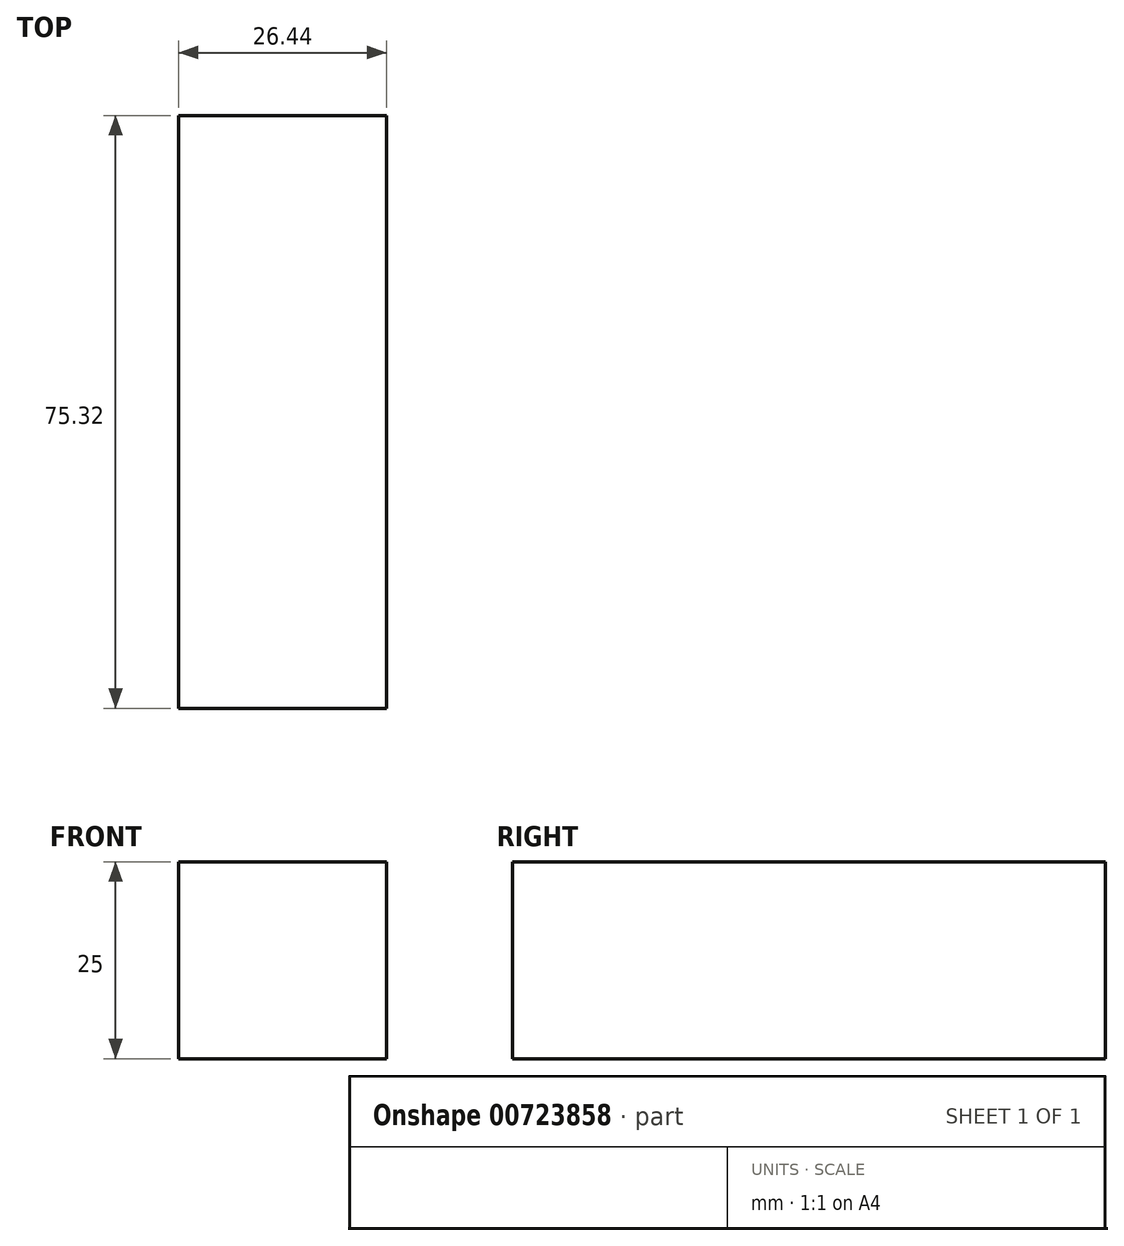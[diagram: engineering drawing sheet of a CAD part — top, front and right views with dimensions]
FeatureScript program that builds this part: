
annotation { "Feature Type Name" : "Feature", "Feature Type Description" : "" }
export const myFeature = defineFeature(function(context is Context, id is Id, definition is map)
    precondition{}
    {
        {
            var Q0;
            Q0=qCreatedBy(makeId("Top.planeOp"),FACE);
            var sketch = newSketch(context, id + "F0", { "sketchPlane" : qUnion([Q0])});
            skLineSegment(sketch, "E0.bottom", {"start": v(-34.36, 31.4) * mm, "end": v(-7.92, 31.4) * mm});
            skLineSegment(sketch, "E0.top", {"start": v(-34.36, 106.72) * mm, "end": v(-7.92, 106.72) * mm});
            skLineSegment(sketch, "E0.left", {"start": v(-34.36, 31.4) * mm, "end": v(-34.36, 106.72) * mm});
            skLineSegment(sketch, "E0.right", {"start": v(-7.92, 31.4) * mm, "end": v(-7.92, 106.72) * mm});
            skSolve(sketch);
        }
        {
            var Q0;
            Q0=makeQuery(id+"F0.imprint","IMPRINT",FACE,{"disambiguationData":[TD([[makeQuery(id+"F0.imprint","IMPRINT",EDGE,{"derivedFrom":sQuery(id+"F0.wireOp",EDGE,"E0.bottom")}),1.0]])]});
            extrude(context, id + "F1", {"entities" : qUnion([Q0]), "depth" : 25 * mm, "offsetDistance" : 25 * mm});
        }
    });
